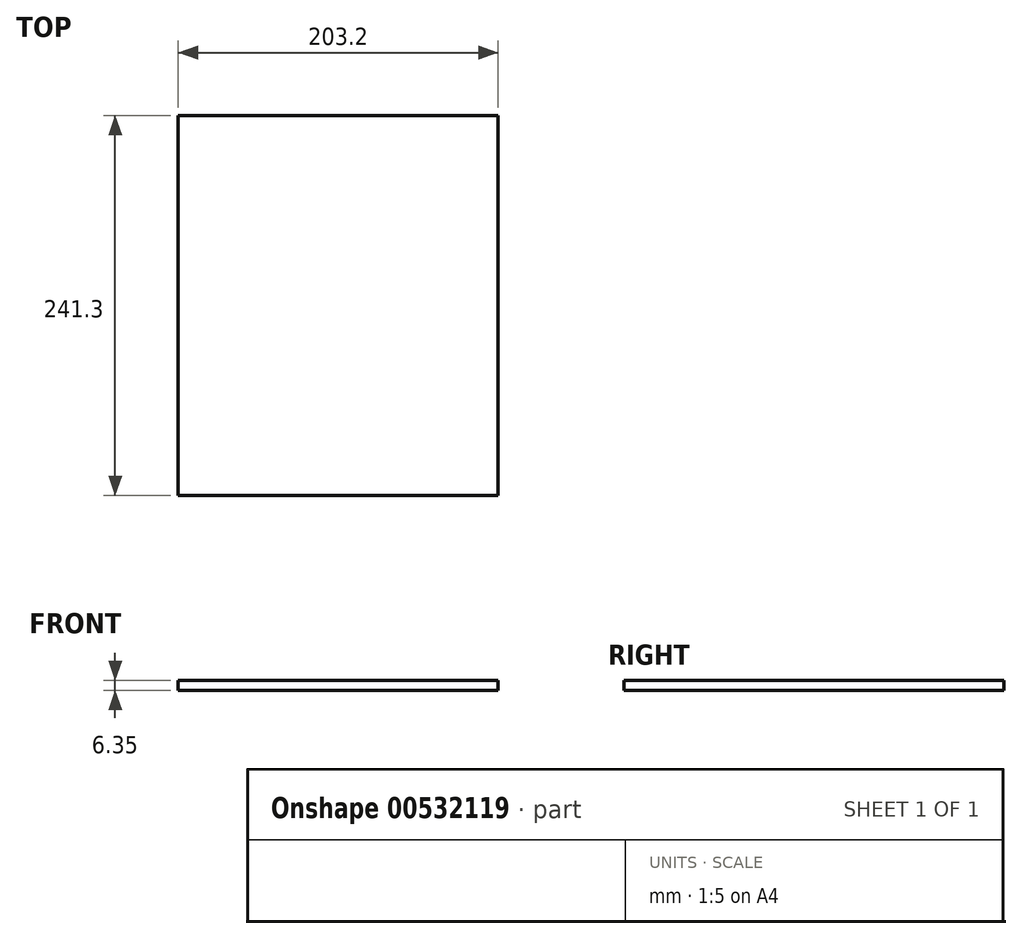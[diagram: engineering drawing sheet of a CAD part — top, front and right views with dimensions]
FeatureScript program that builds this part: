
annotation { "Feature Type Name" : "Feature", "Feature Type Description" : "" }
export const myFeature = defineFeature(function(context is Context, id is Id, definition is map)
    precondition{}
    {
        {
            var Q0;
            Q0=qCreatedBy(makeId("Top.planeOp"),FACE);
            var sketch = newSketch(context, id + "F0", { "sketchPlane" : qUnion([Q0])});
            skLineSegment(sketch, "E0.bottom", {"start": v(101.6, -120.65) * mm, "end": v(-101.6, -120.65) * mm});
            skLineSegment(sketch, "E0.top", {"start": v(101.6, 120.65) * mm, "end": v(-101.6, 120.65) * mm});
            skLineSegment(sketch, "E0.left", {"start": v(101.6, -120.65) * mm, "end": v(101.6, 120.65) * mm});
            skLineSegment(sketch, "E0.right", {"start": v(-101.6, -120.65) * mm, "end": v(-101.6, 120.65) * mm});
            skPoint(sketch, "E0.middle", {"position": v(0, 0) * mm});
            skSolve(sketch);
        }
        {
            var Q0;
            Q0 = qSketchRegion(id + "F0", true);
            extrude(context, id + "F1", {"entities" : qUnion([Q0]), "depth" : 6.35 * mm, "offsetDistance" : 25.4 * mm});
        }
    });
